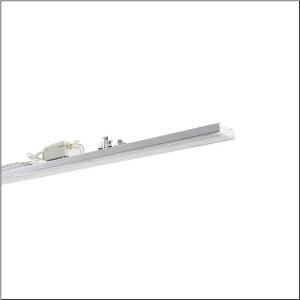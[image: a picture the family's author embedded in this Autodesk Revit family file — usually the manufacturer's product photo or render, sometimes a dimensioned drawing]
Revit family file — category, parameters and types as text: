
# Revit family: licross_11_recessed_ho_51tl11cn4c5s
name_source: partatom
category: Lighting Fixtures
units: mm (PartAtom-declared; Revit-internal decimal feet)

## family parameters
Cut with Voids When Loaded = No
Host = Face
Light Source = No
Part Type = Normal
Room Calculation Point = No
Round Connector Dimension = Use Diameter
Shared = No

## types (1)
- --- (1 x LED, 12710 lm, 66.5 W, 4000K)
    Apparent Load = 67 VA
    CIE Flux Codes = 87 95 99 100 100
    Color Rendering = 80
    Color Temperature = 4000K
    Default Elevation = 1800 mm
    Description = Licross 11 Recessed HO, luminaire insert, of sheet steel, coil coated, white, length: 1.500mm, width: 66mm, height: 67mm, LED rated luminous flux: 12.710lm, light colour: 840, SDCM (Standard Deviation of Colour Matching)MacAdam ≤ 2 SDCM (initial), control gear: ON/OFF Multilumen, CLOi, with plug, 3-pole, with phase selection, mains connection: 220..240V, AC, 50/60Hz, start of lifetime: 67W, end of service life: 75W, internal wiring halogen-free, primary light control with lens, of plastic, primary optical cover: cover, of PMMA, light emission: direct distribution, primary light characteristic: symmetric, protection rating (complete): IP40, insulation class (complete): insulation class I (protective earthing), certification: CE, ENEC, VDE, UKCA, protection symbol: D if used in an environment without relevant dust loads with corresponding accessories, impact resistance: IK06, permissible ambient temperature for indoor applications: -35..+35°C, corresponds to IFS (International Featured Standards) requirements for safety and quality in the food industry, reducing of maximum allowable ambient temperature of 5°C with ceiling mounting, LABS conformity tested according to VDMA 24364:2018-05, The light source and the operating device comply with the requirements of the Ecodesign Regulation (EU) 2019/2020 and are replaceable in accordance with this regulation, packaging unit: 1 piece
    Height = 58 mm
    Lamp = 1 x LED
    Lamp Light Flux = 12710 lm
    Lamp Power = 66.5 W
    Lamp count = 1
    Length = 1500 mm
    Luminous efficacy = 191 lm/W
    Manufacturer = Siteco
    ModVariant = No
    Model = 51TL11CN4C5S
    Mounting Place = Ceiling
    Mounting Type = Pendant
    Number of Poles = 1
    OnlyDefault = Yes
    Power Factor = 1
    Product Name = Licross 11 Recessed HO
    Product group = luminaire insert | ceiling pendant
    ProductGroupID = 901
    Protection Class = Protection class I
    Protection Degree = IP 40
    RLX_Detail_Level = 1
    RLX_Emergency_Light_Flux = 0 lm
    RLX_Emergency_Type = 0
    RLX_Emergency_Type_DB = No
    RlxData = <blob elided: 22537 chars, md5=8da3ba22>
    Socket = socket
    Standby Power = 0 W
    System Light Flux = 12710 lm
    System Power = 67 W
    Type Comments = factory setting: luminous flux: 100 % | (A | C | E) | 156 mA
    Type Image = l_1296930.jpg
    URL = http://relux.com
    VarID = @adj_001547
    Voltage = 0 V
    Weight = 0.00 kg
    Width = 66 mm

## geometry (parser evidence)
native form markers: Blend x4, Sweep x12
no freeform markers — native parametric forms only
